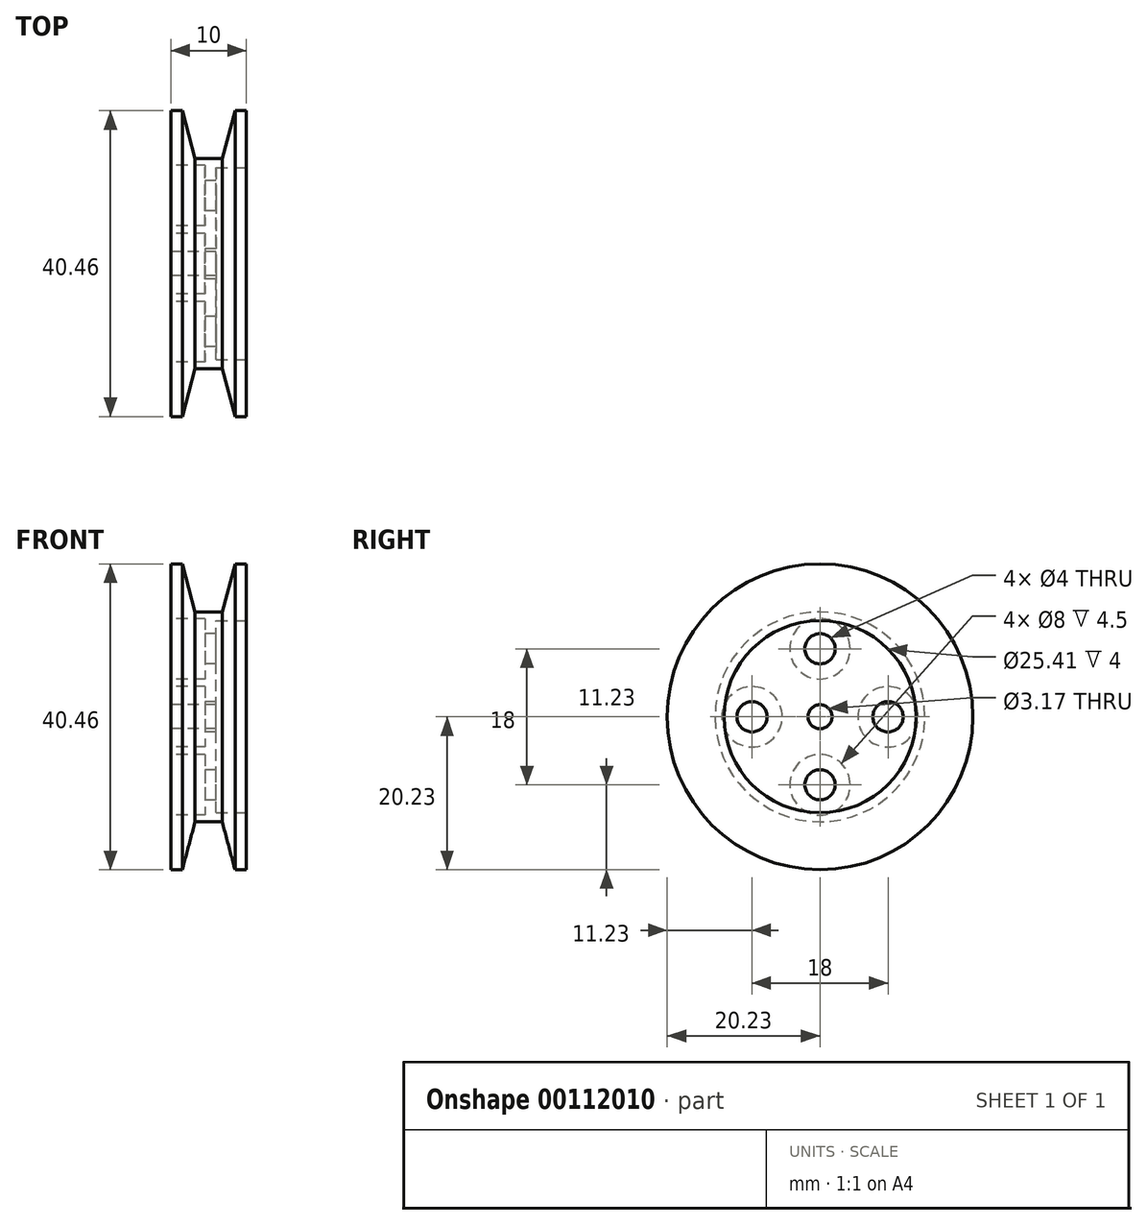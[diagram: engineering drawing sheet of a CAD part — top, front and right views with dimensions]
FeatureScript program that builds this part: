
annotation { "Feature Type Name" : "Feature", "Feature Type Description" : "" }
export const myFeature = defineFeature(function(context is Context, id is Id, definition is map)
    precondition{}
    {
        {
            var Q0;
            Q0=qCreatedBy(makeId("Front.planeOp"),FACE);
            var sketch = newSketch(context, id + "F0", { "sketchPlane" : qUnion([Q0])});
            skLineSegment(sketch, "E0", {"start": v(0, 0) * mm, "end": v(0, 20.23) * mm});
            skLineSegment(sketch, "E1", {"start": v(0, 20.23) * mm, "end": v(1.5, 20.23) * mm});
            skLineSegment(sketch, "E2", {"start": v(1.5, 20.23) * mm, "end": v(3.2, 13.88) * mm});
            skLineSegment(sketch, "E3", {"start": v(3.2, 13.88) * mm, "end": v(6.8, 13.88) * mm});
            skLineSegment(sketch, "E4", {"start": v(6.8, 13.88) * mm, "end": v(8.5, 20.23) * mm});
            skLineSegment(sketch, "E5", {"start": v(8.5, 20.23) * mm, "end": v(10, 20.23) * mm});
            skLineSegment(sketch, "E6", {"start": v(10, 20.23) * mm, "end": v(10, 0) * mm});
            skLineSegment(sketch, "E7", {"start": v(10, 0) * mm, "end": v(0, 0) * mm});
            skLineSegment(sketch, "E8", {"start": v(1.82, 19.05) * mm, "end": v(8.17, 19.05) * mm, "construction": true});
            skPoint(sketch, "E9", {"position": v(5, 13.88) * mm});
            skSolve(sketch);
        }
        {
            var Q0;
            Q0=makeQuery(id+"F0.imprint","IMPRINT",FACE,{"disambiguationData":[TD([[makeQuery(id+"F0.imprint","IMPRINT",EDGE,{"derivedFrom":sQuery(id+"F0.wireOp",EDGE,"E0")}),-1.0]])]});
            var Q1;
            Q1=sQuery(id+"F0.wireOp",EDGE,"E7");
            revolve(context, id + "F1", {"entities" : qUnion([Q0]), "axis" : qUnion([Q1]), "revolveType" : RevolveType.FULL});
        }
        {
            var Q0;
            Q0=makeQuery(id+"F1.opRevolve","SWEPT_FACE",FACE,{"disambiguationData":[OSD([sQuery(id+"F0.wireOp",EDGE,"E6")])]});
            var sketch = newSketch(context, id + "F2", { "sketchPlane" : qUnion([Q0])});
            skCircle(sketch, "E10", {"center": v(0, 0) * mm, "radius": 12.7 * mm});
            skSolve(sketch);
        }
        {
            var Q0;
            Q0 = qSketchRegion(id + "F2", true);
            extrude(context, id + "F3", {"entities" : qUnion([Q0]), "operationType" : NewBodyOperationType.REMOVE, "oppositeDirection" : true, "depth" : 4 * mm});
        }
        {
            var Q0;
            Q0=makeQuery(id+"F1.opRevolve","SWEPT_FACE",FACE,{"disambiguationData":[OSD([sQuery(id+"F0.wireOp",EDGE,"E0")])]});
            var sketch = newSketch(context, id + "F4", { "sketchPlane" : qUnion([Q0])});
            skCircle(sketch, "E11", {"center": v(0, 0) * mm, "radius": 9 * mm, "construction": true});
            skCircle(sketch, "E12", {"center": v(0, 9) * mm, "radius": 4 * mm});
            skCircle(sketch, "E13", {"center": v(9, 0) * mm, "radius": 4 * mm});
            skCircle(sketch, "E14", {"center": v(0, -9) * mm, "radius": 4 * mm});
            skCircle(sketch, "E15", {"center": v(-9, 0) * mm, "radius": 4 * mm});
            skCircle(sketch, "E16", {"center": v(0, 9) * mm, "radius": 2 * mm, "construction": true});
            skSolve(sketch);
        }
        {
            var Q0;
            Q0=sQuery(id+"F4.wireOp",VERTEX,"E12.center");
            var Q1;
            Q1=sQuery(id+"F4.wireOp",VERTEX,"E15.center");
            var Q2;
            Q2=sQuery(id+"F4.wireOp",VERTEX,"E14.center");
            var Q3;
            Q3=sQuery(id+"F4.wireOp",VERTEX,"E13.center");
            var Q4;
            Q4=makeQuery(id+"F1.opRevolve","SWEPT_BODY",BODY,{"disambiguationData":[OSD([sQuery(id+"F0.wireOp",EDGE,"E0"),sQuery(id+"F0.wireOp",EDGE,"E1"),sQuery(id+"F0.wireOp",EDGE,"E2"),sQuery(id+"F0.wireOp",EDGE,"E3"),sQuery(id+"F0.wireOp",EDGE,"E4"),sQuery(id+"F0.wireOp",EDGE,"E5"),sQuery(id+"F0.wireOp",EDGE,"E6"),sQuery(id+"F0.wireOp",EDGE,"E7")])]});
            hole(context, id + "F5", {"style" : HoleStyle.C_BORE, "endStyle" : HoleEndStyle.THROUGH, "holeDiameter" : 4 * mm, "cBoreDiameter" : 8 * mm, "cBoreDepth" : 4.5 * mm, "locations" : qUnion([Q0, Q1, Q2, Q3]), "scope" : qUnion([Q4]), "isTappedThrough" : true});
        }
        {
            var Q0;
            Q0=makeQuery(id+"F1.opRevolve","SWEPT_FACE",FACE,{"disambiguationData":[OSD([sQuery(id+"F0.wireOp",EDGE,"E0")])]});
            var sketch = newSketch(context, id + "F6", { "sketchPlane" : qUnion([Q0])});
            skCircle(sketch, "E17", {"center": v(0, 0) * mm, "radius": 1.59 * mm});
            skSolve(sketch);
        }
        {
            var Q0;
            Q0 = qSketchRegion(id + "F6", true);
            extrude(context, id + "F7", {"entities" : qUnion([Q0]), "operationType" : NewBodyOperationType.REMOVE, "endBound" : BoundingType.THROUGH_ALL, "oppositeDirection" : true, "depth" : 25 * mm});
        }
    });
